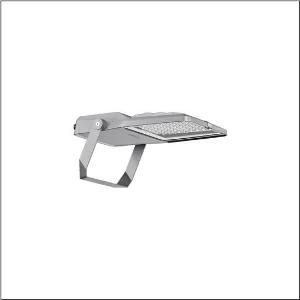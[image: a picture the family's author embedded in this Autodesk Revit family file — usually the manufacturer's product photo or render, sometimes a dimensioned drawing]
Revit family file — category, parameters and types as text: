
# Revit family: floodlight_fl_21_mini___pl52_5xa7776d2d1a_6cb1
name_source: partatom
category: Lighting Fixtures
units: mm (PartAtom-declared; Revit-internal decimal feet)

## family parameters
Cut with Voids When Loaded = No
Host = Face
Light Source = No
Part Type = Normal
Room Calculation Point = No
Round Connector Dimension = Use Diameter
Shared = No

## types (1)
- --- (1 x LED, 17840 lm, 142.9 W, 3000K)
    Apparent Load = 143 VA
    CIE Flux Codes = 26 60 98 100 100
    Color Rendering = 70
    Color Temperature = 3000K
    Default Elevation = 1800 mm
    Description = Floodlight FL 21 mini, floodlight, primary light control with lens, of PMMA, primary optical cover: protective disc, of toughened safety glass, transparent, light distribution: PL52, light emission: direct distribution, installation type: surface-mounted, LED, High Power LED, rated luminous flux: 17.840lm, luminous efficacy: 125lm/W, light colour: 730, colour temperature: 3000K, control: flexible luminous flux parameterisation, time-dependent luminous flux control, constant luminous flux control, overheat protection, presetting dimming logarithmic, with terminal, 6-pole, mains connection: 220..240V, AC, 50/60Hz, start of lifetime: 143W, end of service life: 151W, reduction: 63W, luminaire housing, of diecast aluminium, powder-coated, Siteco® metallic grey (DB 702S), corrosivity category C5 mid according to DIN EN ISO 12944, sealing non-destructively replaceable, mounting bracket, of steel, galvanised, powder-coated, Siteco® metallic grey (DB 702S), Smart Interface below and above, protection rating (complete): IP66, insulation class (complete): insulation class II (safety insulation), certification: CE, ENEC, VDE, protection symbol: D, impact resistance: IK08, permissible operating ambient temperature: -40..+40°C, permissible operating ambient temperature for outdoor applications: -40..+50°C, standard: DIN EN 12944, LABS conformity tested according to VDMA 24364:2018-05, packaging unit: 1 piece

Light Distribution: PL52
    Height = 70 mm
    Lamp = 1 x LED
    Lamp Light Flux = 17840 lm
    Lamp Power = 142.9 W
    Lamp count = 1
    Length = 485 mm
    Luminous efficacy = 125 lm/W
    Manufacturer = Siteco
    ModVariant = No
    Model = 5XA7776D2D1A
    Number of Poles = 1
    OnlyDefault = Yes
    Power Factor = 1
    Product Name = Floodlight FL 21 mini | PL52
    Product group = floodlight | pylon annexe
    ProductGroupID = 6200
    Protection Class = Protection class II
    Protection Degree = IP 66
    RLX_Detail_Level = 1
    RLX_Emergency_Light_Flux = 0 lm
    RLX_Emergency_Type = 0
    RLX_Emergency_Type_DB = No
    RlxData = <blob elided: 96557 chars, md5=7bb54540>
    Socket = socket
    Standby Power = 0 W
    System Light Flux = 17840 lm
    System Power = 143 W
    Type Comments = factory setting: luminous flux: 100 % | dim-lin: 254 | 730 mA
    Type Image = l_1006845.jpg
    URL = http://relux.com
    VarID = @adj_113301
    Voltage = 0 V
    Weight = 0.00 kg
    Width = 337 mm

## geometry (parser evidence)
native form markers: Blend x4, Sweep x10
no freeform markers — native parametric forms only
